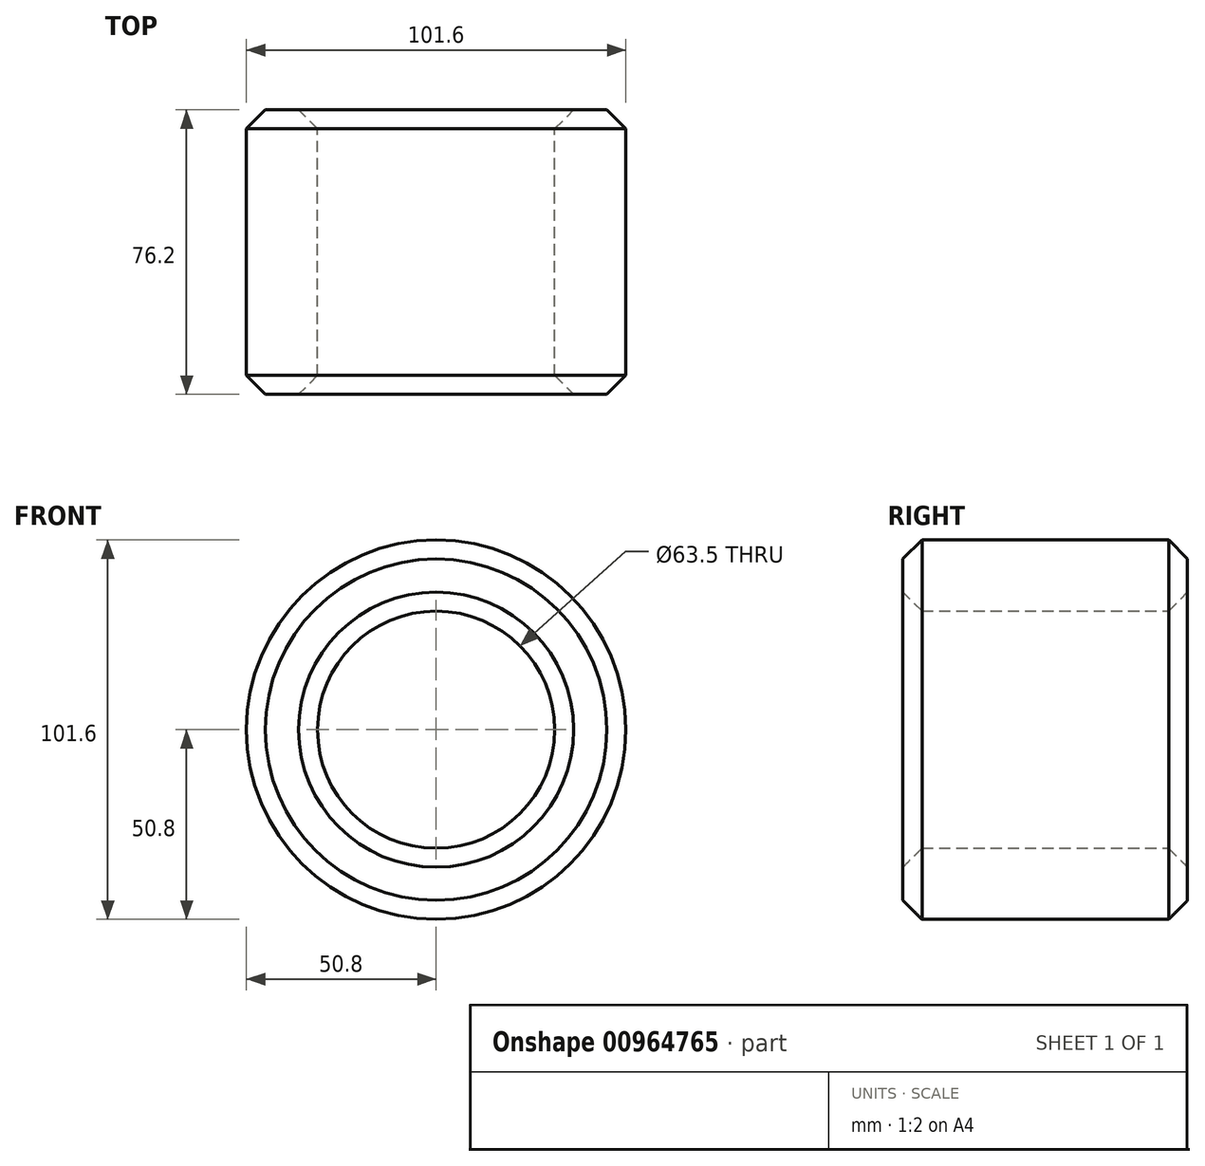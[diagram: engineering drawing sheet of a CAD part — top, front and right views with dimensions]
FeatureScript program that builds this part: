
annotation { "Feature Type Name" : "Feature", "Feature Type Description" : "" }
export const myFeature = defineFeature(function(context is Context, id is Id, definition is map)
    precondition{}
    {
        {
            var Q0;
            Q0=qCreatedBy(makeId("Front.planeOp"),FACE);
            var sketch = newSketch(context, id + "F0", { "sketchPlane" : qUnion([Q0])});
            skCircle(sketch, "E0", {"center": v(0, 0) * mm, "radius": 50.8 * mm});
            skCircle(sketch, "E1", {"center": v(0, 0) * mm, "radius": 31.75 * mm});
            skSolve(sketch);
        }
        {
            var Q0;
            Q0 = qSketchRegion(id + "F0", true);
            extrude(context, id + "F1", {"entities" : qUnion([Q0]), "depth" : 76.2 * mm, "offsetDistance" : 25.4 * mm});
        }
        {
            var Q0;
            Q0=makeQuery(id+"F1.opExtrude","CAP_EDGE",EDGE,{"disambiguationData":[OSD([sQuery(id+"F0.wireOp",EDGE,"E1")])],"isStart":false});
            var Q1;
            Q1=makeQuery(id+"F1.opExtrude","CAP_EDGE",EDGE,{"disambiguationData":[OSD([sQuery(id+"F0.wireOp",EDGE,"E1")])],"isStart":true});
            chamfer(context, id + "F2", {"entities" : qUnion([Q0, Q1]), "width" : 5.08 * mm, "tangentPropagation" : true});
        }
        {
            var Q0;
            Q0=makeQuery(id+"F1.opExtrude","CAP_EDGE",EDGE,{"disambiguationData":[OSD([sQuery(id+"F0.wireOp",EDGE,"E0")])],"isStart":false});
            var Q1;
            Q1=makeQuery(id+"F1.opExtrude","CAP_EDGE",EDGE,{"disambiguationData":[OSD([sQuery(id+"F0.wireOp",EDGE,"E0")])],"isStart":true});
            chamfer(context, id + "F3", {"entities" : qUnion([Q0, Q1]), "width" : 5.08 * mm, "tangentPropagation" : true});
        }
    });
